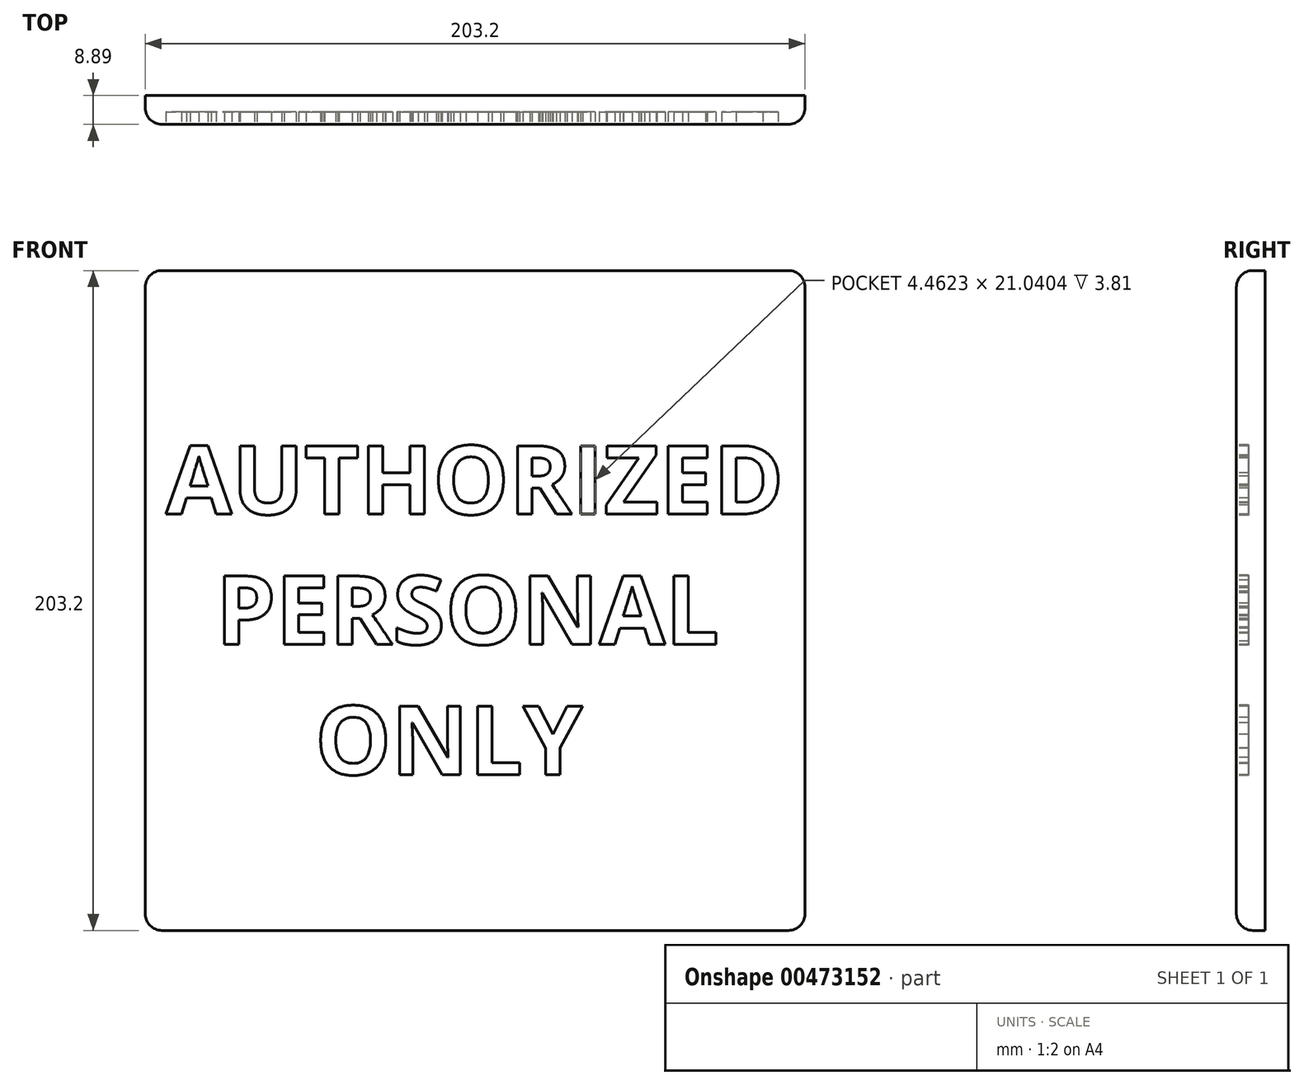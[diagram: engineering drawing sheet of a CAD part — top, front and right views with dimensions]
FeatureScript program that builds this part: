
annotation { "Feature Type Name" : "Feature", "Feature Type Description" : "" }
export const myFeature = defineFeature(function(context is Context, id is Id, definition is map)
    precondition{}
    {
        {
            var Q0;
            Q0=qCreatedBy(makeId("Front.planeOp"),FACE);
            var sketch = newSketch(context, id + "F0", { "sketchPlane" : qUnion([Q0])});
            skLineSegment(sketch, "E0.bottom", {"start": v(101.6, 101.6) * mm, "end": v(-101.6, 101.6) * mm});
            skLineSegment(sketch, "E0.top", {"start": v(101.6, -101.6) * mm, "end": v(-101.6, -101.6) * mm});
            skLineSegment(sketch, "E0.left", {"start": v(101.6, 101.6) * mm, "end": v(101.6, -101.6) * mm});
            skLineSegment(sketch, "E0.right", {"start": v(-101.6, 101.6) * mm, "end": v(-101.6, -101.6) * mm});
            skPoint(sketch, "E0.middle", {"position": v(0, 0) * mm});
            skSolve(sketch);
        }
        {
            var Q0;
            Q0 = qSketchRegion(id + "F0", true);
            extrude(context, id + "F1", {"entities" : qUnion([Q0]), "depth" : 8.9 * mm});
        }
        {
            var Q0;
            Q0=makeQuery(id+"F1.opExtrude","CAP_FACE",FACE,{"disambiguationData":[OSD([sQuery(id+"F0.wireOp",EDGE,"E0.bottom"),sQuery(id+"F0.wireOp",EDGE,"E0.top"),sQuery(id+"F0.wireOp",EDGE,"E0.left"),sQuery(id+"F0.wireOp",EDGE,"E0.right")])],"isStart":false});
            var sketch = newSketch(context, id + "F2", { "sketchPlane" : qUnion([Q0])});
            skText(sketch, "E1", { "text": "AUTHORIZED\n  PERSONAL\n      ONLY\n", "fontName": "OpenSans-Bold.ttf"});
            const initialGuessF2  = {"E1": [-0.09525, 0.02656, 1, 0, 0.02122]};
            skSetInitialGuess(sketch, initialGuessF2);
            skSolve(sketch);
        }
        {
            var Q0;
            Q0=makeQuery(id+"F1.opExtrude","SWEPT_EDGE",EDGE,{"disambiguationData":[OSD([sQuery(id+"F0.wireOp",EDGE,"E0.bottom"),sQuery(id+"F0.wireOp",EDGE,"E0.left")])]});
            fillet(context, id + "F3", {"entities" : qUnion([Q0]), "radius" : 5.08 * mm, "tangentPropagation" : true, "allowEdgeOverflow" : false});
        }
        {
            var Q0;
            Q0=makeQuery(id+"F1.opExtrude","SWEPT_EDGE",EDGE,{"disambiguationData":[OSD([sQuery(id+"F0.wireOp",EDGE,"E0.bottom"),sQuery(id+"F0.wireOp",EDGE,"E0.right")])]});
            fillet(context, id + "F4", {"entities" : qUnion([Q0]), "radius" : 5.08 * mm, "tangentPropagation" : true, "allowEdgeOverflow" : false});
        }
        {
            var Q0;
            Q0=makeQuery(id+"F1.opExtrude","SWEPT_EDGE",EDGE,{"disambiguationData":[OSD([sQuery(id+"F0.wireOp",EDGE,"E0.top"),sQuery(id+"F0.wireOp",EDGE,"E0.right")])]});
            fillet(context, id + "F5", {"entities" : qUnion([Q0]), "radius" : 5.08 * mm, "tangentPropagation" : true, "allowEdgeOverflow" : false});
        }
        {
            var Q0;
            Q0=makeQuery(id+"F1.opExtrude","SWEPT_EDGE",EDGE,{"disambiguationData":[OSD([sQuery(id+"F0.wireOp",EDGE,"E0.top"),sQuery(id+"F0.wireOp",EDGE,"E0.left")])]});
            fillet(context, id + "F6", {"entities" : qUnion([Q0]), "radius" : 5.08 * mm, "tangentPropagation" : true, "allowEdgeOverflow" : false});
        }
        {
            var Q0;
            Q0=makeQuery(id+"F1.opExtrude","CAP_EDGE",EDGE,{"disambiguationData":[OSD([sQuery(id+"F0.wireOp",EDGE,"E0.top")])],"isStart":false});
            fillet(context, id + "F7", {"entities" : qUnion([Q0]), "radius" : 5.08 * mm, "tangentPropagation" : true, "allowEdgeOverflow" : false});
        }
        {
            var Q0;
            Q0 = qSketchRegion(id + "F2", true);
            extrude(context, id + "F8", {"entities" : qUnion([Q0]), "operationType" : NewBodyOperationType.REMOVE, "oppositeDirection" : true, "depth" : 3.8 * mm});
        }
    });
